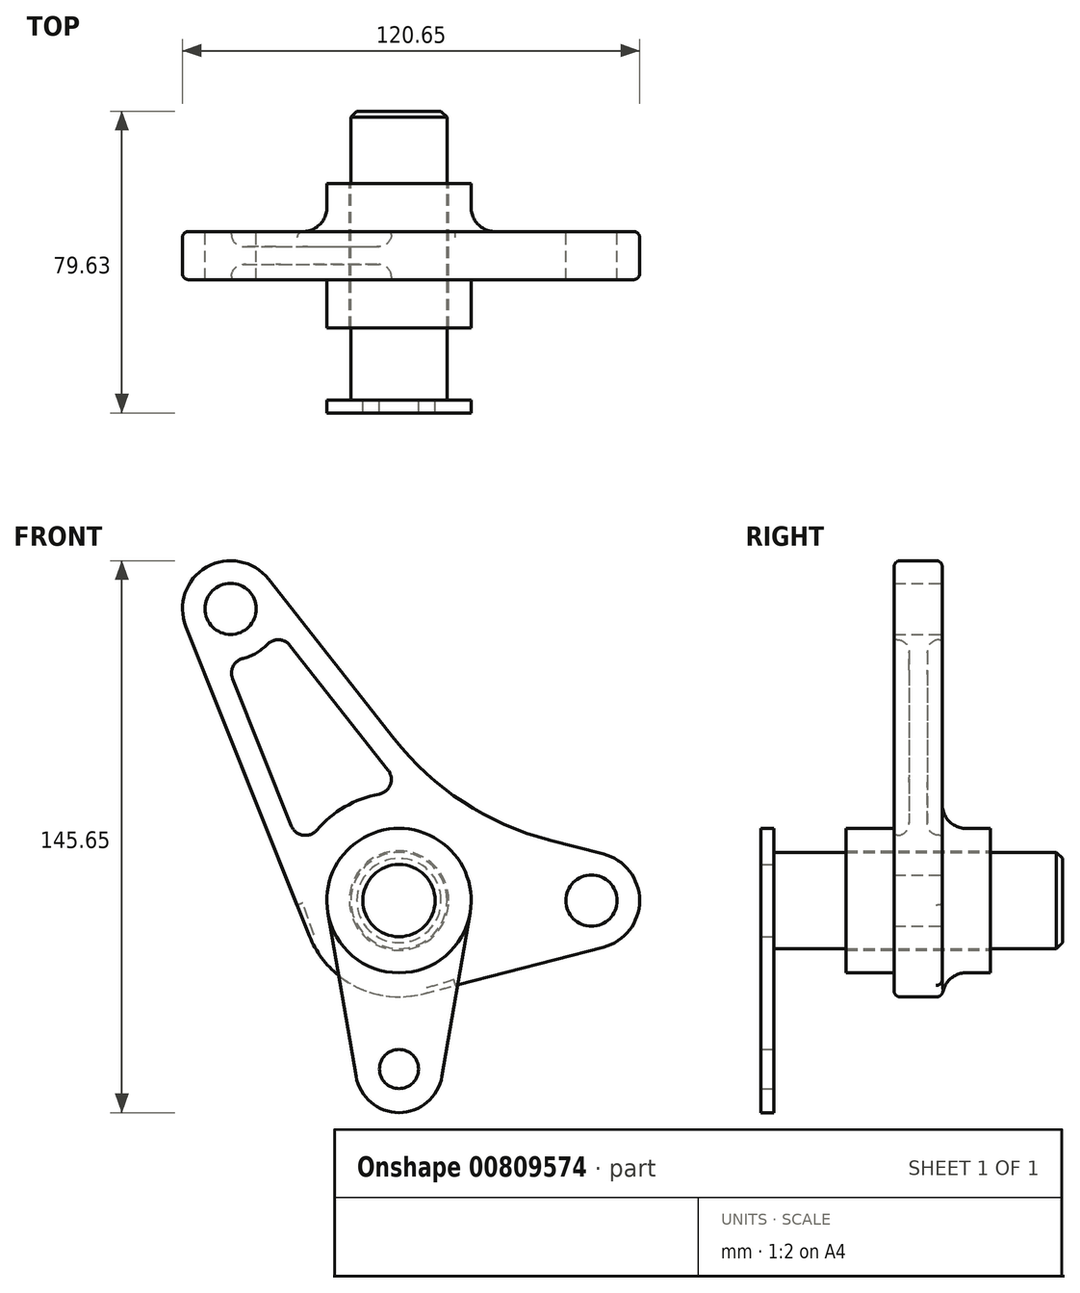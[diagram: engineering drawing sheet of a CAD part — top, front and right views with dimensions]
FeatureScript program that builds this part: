
annotation { "Feature Type Name" : "Feature", "Feature Type Description" : "" }
export const myFeature = defineFeature(function(context is Context, id is Id, definition is map)
    precondition{}
    {
        {
            var Q0;
            Q0=qCreatedBy(makeId("Front.planeOp"),FACE);
            var sketch = newSketch(context, id + "F0", { "sketchPlane" : qUnion([Q0])});
            skCircle(sketch, "E0", {"center": v(0, 0) * mm, "radius": 13.1 * mm});
            skCircle(sketch, "E1", {"center": v(50.8, 0) * mm, "radius": 6.75 * mm});
            skCircle(sketch, "E2", {"center": v(-44.45, 76.99) * mm, "radius": 6.75 * mm});
            skLineSegment(sketch, "E3", {"start": v(0, 0) * mm, "end": v(-44.45, 76.99) * mm});
            skArc(sketch, "E4", {"start": v(-34.47, 84.85) * mm, "mid": v(-50.8, 87.99) * mm, "end": v(-56.24, 72.28) * mm});
            skCircle(sketch, "E5", {"center": v(0, 0) * mm, "radius": 25.4 * mm});
            skArc(sketch, "E6", {"start": v(53.98, -12.3) * mm, "mid": v(63.5, 0) * mm, "end": v(53.98, 12.3) * mm});
            skLineSegment(sketch, "E7", {"start": v(-1.26, 42.66) * mm, "end": v(-34.47, 84.85) * mm});
            skLineSegment(sketch, "E8", {"start": v(-56.24, 72.28) * mm, "end": v(-23.59, -9.43) * mm});
            skLineSegment(sketch, "E9", {"start": v(6.35, -24.6) * mm, "end": v(53.97, -12.3) * mm});
            skLineSegment(sketch, "E10", {"start": v(53.97, 12.3) * mm, "end": v(39.56, 16.02) * mm});
            skPoint(sketch, "E11.visualSharp", {"position": v(14.65, 22.45) * mm});
            skArc(sketch, "E11.filletArc", {"start": v(-1.26, 42.66) * mm, "mid": v(16.96, 25.99) * mm, "end": v(39.56, 16.02) * mm});
            skCircle(sketch, "E12", {"center": v(0, 0) * mm, "radius": 19.05 * mm});
            skCircle(sketch, "E13", {"center": v(0, 0) * mm, "radius": 12.7 * mm});
            skSolve(sketch);
        }
        {
            var Q0;
            Q0 = qSketchRegion(id + "F0", true);
            extrude(context, id + "F1", {"entities" : qUnion([Q0]), "endBound" : BoundingType.SYMMETRIC, "depth" : 12.7 * mm, "offsetDistance" : 25.4 * mm});
        }
        {
            var Q0;
            Q0=makeQuery(id+"F0.imprint","IMPRINT",FACE,{"disambiguationData":[TD([[makeQuery(id+"F0.imprint","IMPRINT",EDGE,{"derivedFrom":sQuery(id+"F0.wireOp",EDGE,"E0")}),-1.0]])]});
            extrude(context, id + "F2", {"entities" : qUnion([Q0]), "operationType" : NewBodyOperationType.ADD, "endBound" : BoundingType.SYMMETRIC, "depth" : 38.1 * mm, "offsetDistance" : 25.4 * mm});
        }
        {
            var Q0;
            Q0=makeQuery(id+"F1.opExtrude","CAP_EDGE",EDGE,{"disambiguationData":[OSD([sQuery(id+"F0.wireOp",EDGE,"E12")])],"isStart":false});
            var Q1;
            Q1=makeQuery(id+"F1.opExtrude","CAP_EDGE",EDGE,{"disambiguationData":[OSD([sQuery(id+"F0.wireOp",EDGE,"E12")])],"isStart":true});
            fillet(context, id + "F3", {"entities" : qUnion([Q0, Q1]), "radius" : 6.35 * mm, "tangentPropagation" : true, "allowEdgeOverflow" : false});
        }
        {
            var Q0;
            Q0=makeQuery(id+"F1.opExtrude","CAP_FACE",FACE,{"disambiguationData":[OSD([sQuery(id+"F0.wireOp",EDGE,"E1"),sQuery(id+"F0.wireOp",EDGE,"E2"),sQuery(id+"F0.wireOp",EDGE,"E4"),sQuery(id+"F0.wireOp",EDGE,"E5"),sQuery(id+"F0.wireOp",EDGE,"E6"),sQuery(id+"F0.wireOp",EDGE,"E7"),sQuery(id+"F0.wireOp",EDGE,"E8"),sQuery(id+"F0.wireOp",EDGE,"E9"),sQuery(id+"F0.wireOp",EDGE,"E10"),sQuery(id+"F0.wireOp",EDGE,"E11.filletArc"),sQuery(id+"F0.wireOp",EDGE,"E12")])],"isStart":true});
            var sketch = newSketch(context, id + "F4", { "sketchPlane" : qUnion([Q0])});
            skArc(sketch, "E14", {"start": v(21.7, 18.6) * mm, "mid": v(14.29, 24.75) * mm, "end": v(5.26, 28.09) * mm});
            skArc(sketch, "E15", {"start": v(34.74, 67.62) * mm, "mid": v(37.7, 65.3) * mm, "end": v(41.2, 63.9) * mm});
            skLineSegment(sketch, "E16", {"start": v(28.76, 67.33) * mm, "end": v(2.87, 34.44) * mm});
            skLineSegment(sketch, "E17", {"start": v(43.93, 58.57) * mm, "end": v(28.4, 19.7) * mm});
            skPoint(sketch, "E18.visualSharp", {"position": v(9.78, -26.85) * mm});
            skArc(sketch, "E18.filletArc", {"start": v(21.7, 18.6) * mm, "mid": v(25.36, 17.27) * mm, "end": v(28.4, 19.7) * mm});
            skPoint(sketch, "E19.visualSharp", {"position": v(-28.14, -4.95) * mm});
            skArc(sketch, "E19.filletArc", {"start": v(2.87, 34.44) * mm, "mid": v(2.27, 30.6) * mm, "end": v(5.26, 28.09) * mm});
            skPoint(sketch, "E20.visualSharp", {"position": v(32.1, 71.56) * mm});
            skArc(sketch, "E20.filletArc", {"start": v(34.74, 67.62) * mm, "mid": v(31.68, 68.83) * mm, "end": v(28.76, 67.33) * mm});
            skPoint(sketch, "E21.visualSharp", {"position": v(54.77, 85.69) * mm});
            skArc(sketch, "E21.filletArc", {"start": v(43.93, 58.57) * mm, "mid": v(43.77, 61.85) * mm, "end": v(41.2, 63.9) * mm});
            skSolve(sketch);
        }
        {
            var Q0;
            Q0 = qSketchRegion(id + "F4", true);
            extrude(context, id + "F5", {"entities" : qUnion([Q0]), "operationType" : NewBodyOperationType.REMOVE, "oppositeDirection" : true, "depth" : 3.97 * mm, "offsetDistance" : 25.4 * mm});
        }
        {
            var Q0;
            Q0=makeQuery(id+"F1.opExtrude","CAP_FACE",FACE,{"disambiguationData":[OSD([sQuery(id+"F0.wireOp",EDGE,"E1"),sQuery(id+"F0.wireOp",EDGE,"E2"),sQuery(id+"F0.wireOp",EDGE,"E4"),sQuery(id+"F0.wireOp",EDGE,"E5"),sQuery(id+"F0.wireOp",EDGE,"E6"),sQuery(id+"F0.wireOp",EDGE,"E7"),sQuery(id+"F0.wireOp",EDGE,"E8"),sQuery(id+"F0.wireOp",EDGE,"E9"),sQuery(id+"F0.wireOp",EDGE,"E10"),sQuery(id+"F0.wireOp",EDGE,"E11.filletArc"),sQuery(id+"F0.wireOp",EDGE,"E12")])],"isStart":false});
            var sketch = newSketch(context, id + "F6", { "sketchPlane" : qUnion([Q0])});
            skArc(sketch, "E22", {"start": v(-5.26, 28.09) * mm, "mid": v(-14.29, 24.75) * mm, "end": v(-21.7, 18.6) * mm});
            skArc(sketch, "E23", {"start": v(-41.2, 63.9) * mm, "mid": v(-37.7, 65.3) * mm, "end": v(-34.74, 67.62) * mm});
            skLineSegment(sketch, "E24", {"start": v(-43.93, 58.57) * mm, "end": v(-28.4, 19.7) * mm});
            skLineSegment(sketch, "E25", {"start": v(-28.76, 67.33) * mm, "end": v(-2.87, 34.44) * mm});
            skPoint(sketch, "E26.visualSharp", {"position": v(1.8, 28.52) * mm});
            skArc(sketch, "E26.filletArc", {"start": v(-5.26, 28.09) * mm, "mid": v(-2.27, 30.6) * mm, "end": v(-2.87, 34.44) * mm});
            skPoint(sketch, "E27.visualSharp", {"position": v(-25.6, 12.7) * mm});
            skArc(sketch, "E27.filletArc", {"start": v(-28.4, 19.7) * mm, "mid": v(-25.36, 17.27) * mm, "end": v(-21.7, 18.6) * mm});
            skPoint(sketch, "E28.visualSharp", {"position": v(-45.93, 63.58) * mm});
            skArc(sketch, "E28.filletArc", {"start": v(-41.2, 63.9) * mm, "mid": v(-43.77, 61.85) * mm, "end": v(-43.93, 58.57) * mm});
            skPoint(sketch, "E29.visualSharp", {"position": v(-32.1, 71.56) * mm});
            skArc(sketch, "E29.filletArc", {"start": v(-28.76, 67.33) * mm, "mid": v(-31.68, 68.83) * mm, "end": v(-34.74, 67.62) * mm});
            skSolve(sketch);
        }
        {
            var Q0;
            Q0 = qSketchRegion(id + "F6", true);
            extrude(context, id + "F7", {"entities" : qUnion([Q0]), "operationType" : NewBodyOperationType.REMOVE, "oppositeDirection" : true, "depth" : 3.97 * mm, "offsetDistance" : 25.4 * mm});
        }
        {
            var Q0;
            Q0=makeQuery(id+"F7.boolean.opBoolean","COPY",FACE,{"derivedFrom":makeQuery(id+"F7.opExtrude","CAP_FACE",FACE,{"disambiguationData":[OSD([sQuery(id+"F6.wireOp",EDGE,"E22"),sQuery(id+"F6.wireOp",EDGE,"E23"),sQuery(id+"F6.wireOp",EDGE,"E24"),sQuery(id+"F6.wireOp",EDGE,"E25"),sQuery(id+"F6.wireOp",EDGE,"E26.filletArc"),sQuery(id+"F6.wireOp",EDGE,"E27.filletArc"),sQuery(id+"F6.wireOp",EDGE,"E28.filletArc"),sQuery(id+"F6.wireOp",EDGE,"E29.filletArc")])],"isStart":false})});
            var Q1;
            Q1=makeQuery(id+"F5.boolean.opBoolean","COPY",FACE,{"derivedFrom":makeQuery(id+"F5.opExtrude","CAP_FACE",FACE,{"disambiguationData":[OSD([sQuery(id+"F4.wireOp",EDGE,"E14"),sQuery(id+"F4.wireOp",EDGE,"E15"),sQuery(id+"F4.wireOp",EDGE,"E16"),sQuery(id+"F4.wireOp",EDGE,"E17"),sQuery(id+"F4.wireOp",EDGE,"E18.filletArc"),sQuery(id+"F4.wireOp",EDGE,"E19.filletArc"),sQuery(id+"F4.wireOp",EDGE,"E20.filletArc"),sQuery(id+"F4.wireOp",EDGE,"E21.filletArc")])],"isStart":false})});
            fillet(context, id + "F8", {"entities" : qUnion([Q0, Q1]), "radius" : 3.17 * mm, "tangentPropagation" : true, "allowEdgeOverflow" : false});
        }
        {
            var Q0;
            Q0=makeQuery(id+"F1.opExtrude","CAP_EDGE",EDGE,{"disambiguationData":[OSD([sQuery(id+"F0.wireOp",EDGE,"E11.filletArc")])],"isStart":false});
            var Q1;
            Q1=makeQuery(id+"F1.opExtrude","CAP_EDGE",EDGE,{"disambiguationData":[OSD([sQuery(id+"F0.wireOp",EDGE,"E7")])],"isStart":true});
            var Q2;
            Q2=makeQuery(id+"F7.boolean.opBoolean","COPY",EDGE,{"derivedFrom":makeQuery(id+"F7.opExtrude","CAP_EDGE",EDGE,{"disambiguationData":[OSD([sQuery(id+"F6.wireOp",EDGE,"E25")])],"isStart":true})});
            var Q3;
            Q3=makeQuery(id+"F5.boolean.opBoolean","COPY",EDGE,{"derivedFrom":makeQuery(id+"F5.opExtrude","CAP_EDGE",EDGE,{"disambiguationData":[OSD([sQuery(id+"F4.wireOp",EDGE,"E16")])],"isStart":true})});
            fillet(context, id + "F9", {"entities" : qUnion([Q0, Q1, Q2, Q3]), "radius" : 1.59 * mm, "tangentPropagation" : true, "allowEdgeOverflow" : false});
        }
        {
            var Q0;
            Q0=makeQuery(id+"F0.imprint","IMPRINT",FACE,{"disambiguationData":[TD([[makeQuery(id+"F0.imprint","IMPRINT",EDGE,{"derivedFrom":sQuery(id+"F0.wireOp",EDGE,"E13")}),1.0]])]});
            extrude(context, id + "F10", {"entities" : qUnion([Q0]), "endBound" : BoundingType.SYMMETRIC, "depth" : 76.2 * mm, "offsetDistance" : 25.4 * mm});
        }
        {
            var Q0;
            Q0=makeQuery(id+"F10.opExtrude","CAP_FACE",FACE,{"disambiguationData":[OSD([sQuery(id+"F0.wireOp",EDGE,"E13")])],"isStart":false});
            var sketch = newSketch(context, id + "F11", { "sketchPlane" : qUnion([Q0])});
            skCircle(sketch, "E30", {"center": v(0, 0) * mm, "radius": 9.52 * mm});
            skArc(sketch, "E31", {"start": v(18.77, -3.23) * mm, "mid": v(0, 19.05) * mm, "end": v(-18.77, -3.23) * mm});
            skCircle(sketch, "E32", {"center": v(0, -44.45) * mm, "radius": 5.16 * mm});
            skArc(sketch, "E33", {"start": v(-11.34, -46.4) * mm, "mid": v(0, -55.96) * mm, "end": v(11.34, -46.4) * mm});
            skLineSegment(sketch, "E34", {"start": v(18.77, -3.23) * mm, "end": v(11.34, -46.4) * mm});
            skLineSegment(sketch, "E35", {"start": v(-18.77, -3.23) * mm, "end": v(-11.34, -46.4) * mm});
            skSolve(sketch);
        }
        {
            var Q0;
            Q0 = qSketchRegion(id + "F11", true);
            extrude(context, id + "F12", {"entities" : qUnion([Q0]), "operationType" : NewBodyOperationType.ADD, "depth" : 3.43 * mm, "offsetDistance" : 25.4 * mm});
        }
        {
            var Q0;
            Q0=makeQuery(id+"F10.opExtrude","CAP_EDGE",EDGE,{"disambiguationData":[OSD([sQuery(id+"F0.wireOp",EDGE,"E13")])],"isStart":true});
            chamfer(context, id + "F13", {"entities" : qUnion([Q0]), "width" : 1.59 * mm, "tangentPropagation" : true});
        }
    });
